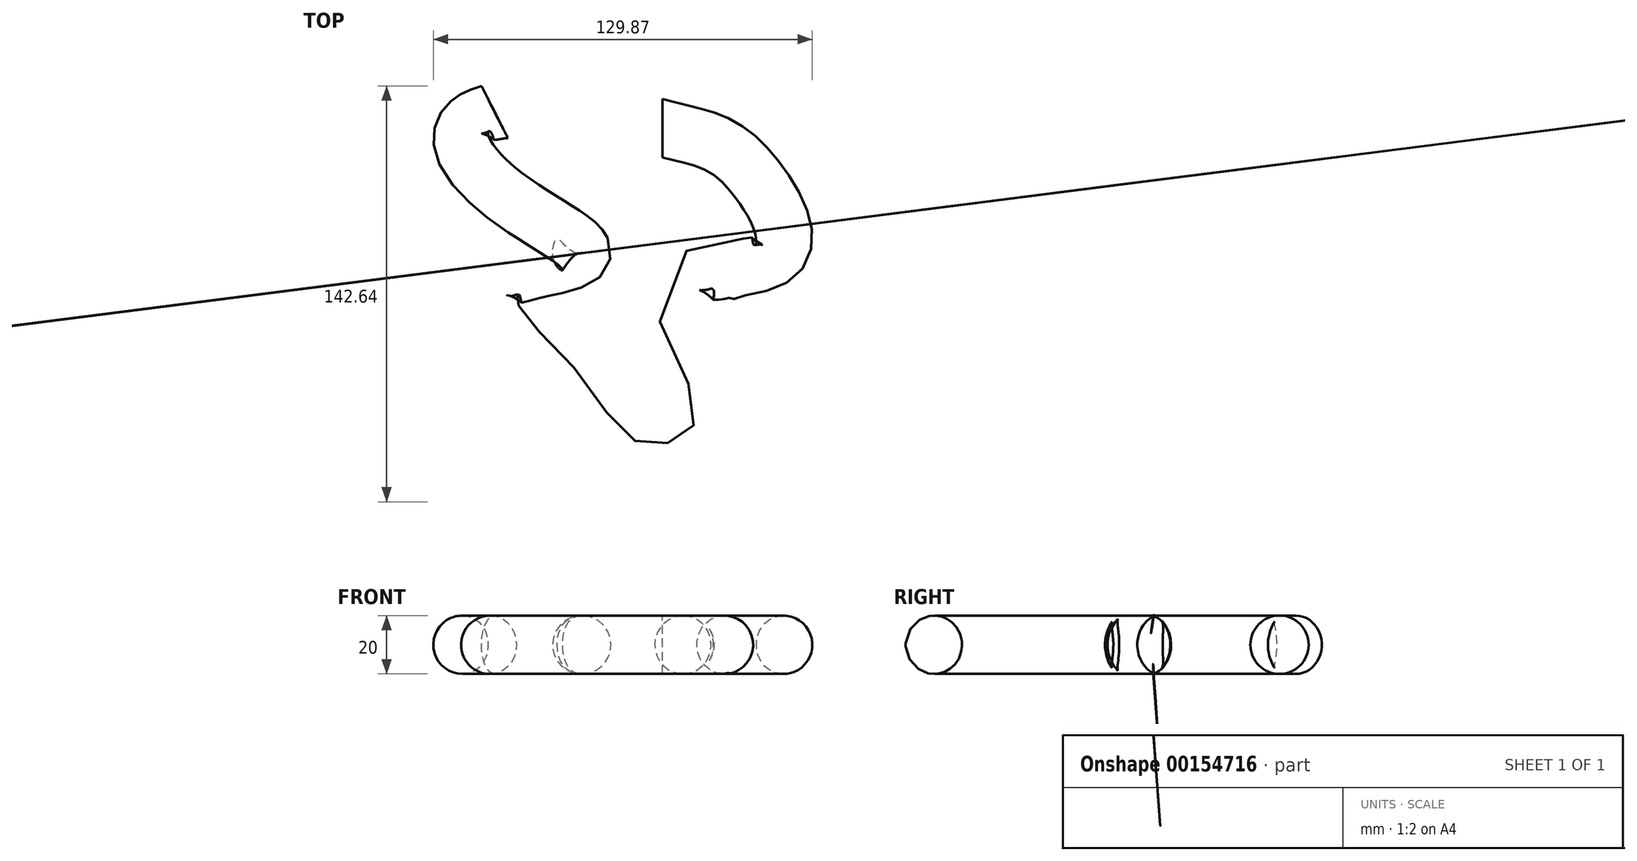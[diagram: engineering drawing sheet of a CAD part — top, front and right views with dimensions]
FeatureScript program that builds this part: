
annotation { "Feature Type Name" : "Feature", "Feature Type Description" : "" }
export const myFeature = defineFeature(function(context is Context, id is Id, definition is map)
    precondition{}
    {
        {
            var Q0;
            Q0=qCreatedBy(makeId("Top.planeOp"),FACE);
            var sketch = newSketch(context, id + "F0", { "sketchPlane" : qUnion([Q0])});
            skLineSegment(sketch, "E0.bottom", {"start": v(30, -25) * mm, "end": v(-30, -25) * mm});
            skLineSegment(sketch, "E0.top", {"start": v(30, 25) * mm, "end": v(-30, 25) * mm});
            skLineSegment(sketch, "E0.left", {"start": v(30, -25) * mm, "end": v(30, 25) * mm});
            skLineSegment(sketch, "E0.right", {"start": v(-30, -25) * mm, "end": v(-30, 25) * mm});
            skPoint(sketch, "E0.middle", {"position": v(0, 0) * mm});
            skSolve(sketch);
        }
        {
            var Q0;
            Q0=qCreatedBy(makeId("Top.planeOp"),FACE);
            cPlane(context, id + "F1", {"entities" : qUnion([Q0]), "cplaneType" : CPlaneType.OFFSET, "offset" : 60 * mm, "width" : 150 * mm, "height" : 150 * mm});
        }
        {
            var Q0;
            Q0=qCreatedBy(id+"F1.planeOp",FACE);
            var sketch = newSketch(context, id + "F2", { "sketchPlane" : qUnion([Q0])});
            skLineSegment(sketch, "E1", {"start": v(0, 15.48) * mm, "end": v(21.5, -13.44) * mm});
            skLineSegment(sketch, "E2.MirrorCS", {"start": v(0, 15.48) * mm, "end": v(-21.5, -13.44) * mm});
            skLineSegment(sketch, "E3", {"start": v(-21.5, -13.44) * mm, "end": v(21.5, -13.44) * mm});
            skSolve(sketch);
        }
        {
            var Q0;
            Q0=makeQuery(id+"F0.imprint","IMPRINT",FACE,{"disambiguationData":[TD([[makeQuery(id+"F0.imprint","IMPRINT",EDGE,{"derivedFrom":sQuery(id+"F0.wireOp",EDGE,"E0.bottom")}),-1.0]])]});
            var Q1;
            Q1=makeQuery(id+"F2.imprint","IMPRINT",FACE,{"disambiguationData":[TD([[makeQuery(id+"F2.imprint","IMPRINT",EDGE,{"derivedFrom":sQuery(id+"F2.wireOp",EDGE,"E1")}),-1.0]])]});
            loft(context, id + "F3", {"bodyType" : ToolBodyType.SURFACE, "wireProfilesArray" : [{ "wireProfileEntities" : qUnion([Q0]) }, { "wireProfileEntities" : qUnion([Q1]) }]});
        }
        {
            var Q0;
            Q0=qCreatedBy(id+"F1.planeOp",FACE);
            cPlane(context, id + "F4", {"entities" : qUnion([Q0]), "cplaneType" : CPlaneType.OFFSET, "offset" : 125 * mm, "width" : 150 * mm, "height" : 150 * mm});
        }
        {
            var Q0;
            Q0=qCreatedBy(id+"F4.planeOp",FACE);
            var sketch = newSketch(context, id + "F5", { "sketchPlane" : qUnion([Q0])});
            skFitSpline(sketch, "E4", {"points": [v(0, 54.08) * mm, v(27.43, 42.18) * mm, v(39.77, 11.35) * mm, v(8.05, 0) * mm, v(21.22, -44.76) * mm, v(-7.94, -63.77) * mm, v(-37.26, -34.93) * mm, v(-54.65, -16.15) * mm, v(-56.88, 0) * mm, v(-27.87, 10.63) * mm, v(-57.78, 34.18) * mm, v(-57.53, 59.68) * mm], "startDerivative": vector(458.18, -116.28) * mm, "endDerivative": vector(666.63, 148.95) * mm});
            skSolve(sketch);
        }
        {
            var Q0;
            Q0=qCreatedBy(makeId("Right.planeOp"),FACE);
            var sketch = newSketch(context, id + "F6", { "sketchPlane" : qUnion([Q0])});
            skCircle(sketch, "E5", {"center": v(54.08, 185) * mm, "radius": 10 * mm});
            skSolve(sketch);
        }
        {
            var Q0;
            Q0=makeQuery(id+"F6.imprint","IMPRINT",FACE,{"disambiguationData":[TD([[makeQuery(id+"F6.imprint","IMPRINT",EDGE,{"derivedFrom":sQuery(id+"F6.wireOp",EDGE,"E5")}),1.0]])]});
            var Q1;
            Q1=sQuery(id+"FC9KyurMV0ucbZw_1.wireOp",EDGE,"hMm5URgq-1GEI-Itmo-iMKn-QCoPPO9tnNRN");
            var Q2;
            Q2=sQuery(id+"F5.wireOp",EDGE,"E4");
            sweep(context, id + "F7", {"profiles" : qUnion([Q0]), "surfaceProfiles" : qUnion([Q1]), "path" : qUnion([Q2])});
        }
    });
